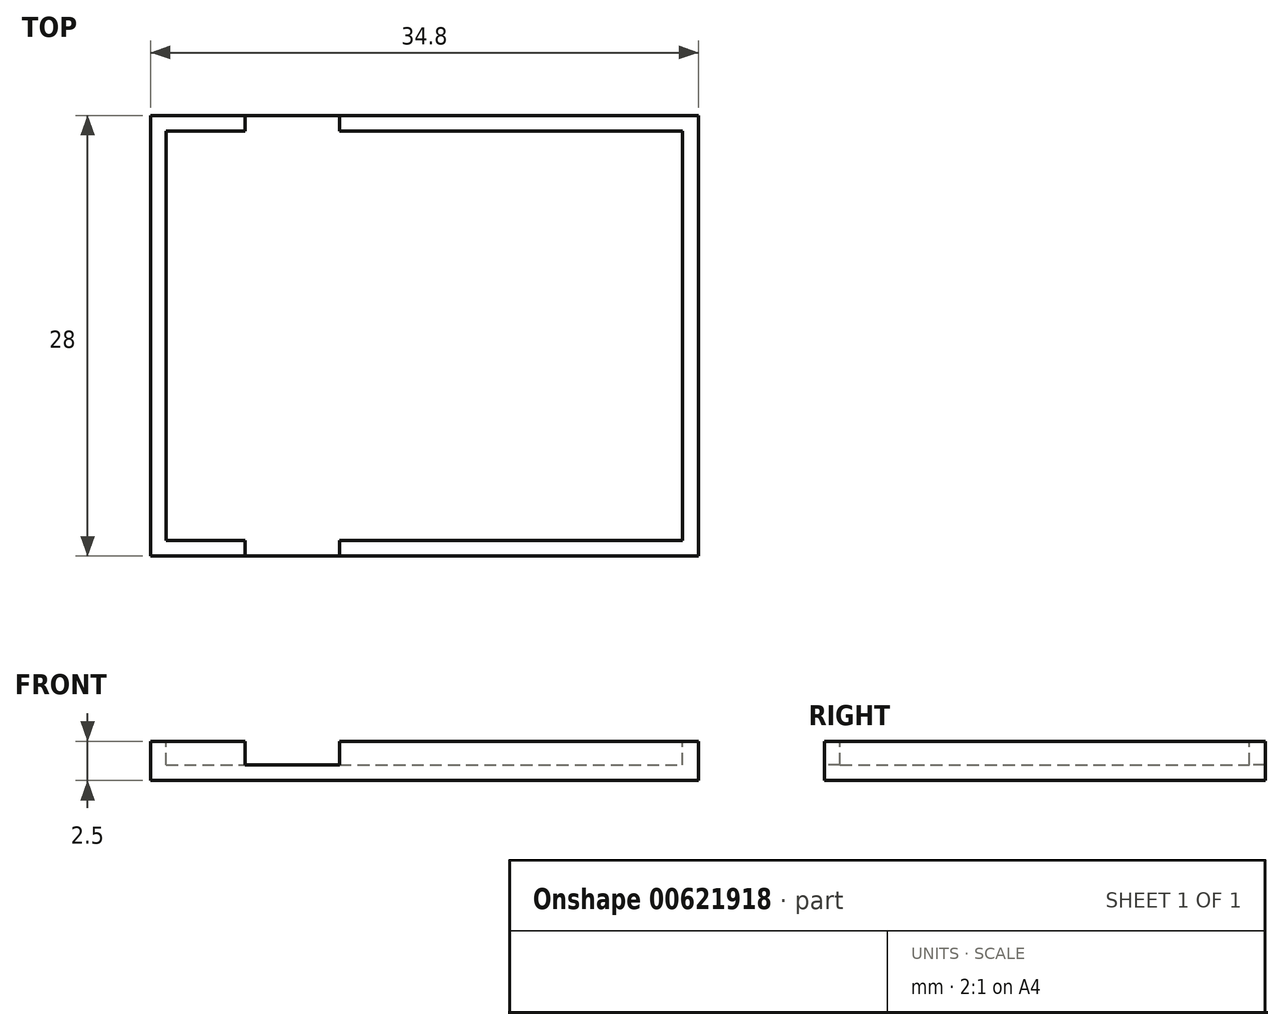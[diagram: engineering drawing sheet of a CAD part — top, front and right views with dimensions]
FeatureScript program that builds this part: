
annotation { "Feature Type Name" : "Feature", "Feature Type Description" : "" }
export const myFeature = defineFeature(function(context is Context, id is Id, definition is map)
    precondition{}
    {
        {
            var Q0;
            Q0=qCreatedBy(makeId("Top.planeOp"),FACE);
            var sketch = newSketch(context, id + "F0", { "sketchPlane" : qUnion([Q0])});
            skLineSegment(sketch, "E0.bottom", {"start": v(-17.4, -14) * mm, "end": v(17.4, -14) * mm});
            skLineSegment(sketch, "E0.top", {"start": v(-17.4, 14) * mm, "end": v(17.4, 14) * mm});
            skLineSegment(sketch, "E0.left", {"start": v(-17.4, -14) * mm, "end": v(-17.4, 14) * mm});
            skLineSegment(sketch, "E0.right", {"start": v(17.4, -14) * mm, "end": v(17.4, 14) * mm});
            skSolve(sketch);
        }
        {
            var Q0;
            Q0=makeQuery(id+"F0.imprint","IMPRINT",FACE,{"disambiguationData":[TD([[makeQuery(id+"F0.imprint","IMPRINT",EDGE,{"derivedFrom":sQuery(id+"F0.wireOp",EDGE,"E0.bottom")}),1.0]])]});
            extrude(context, id + "F1", {"entities" : qUnion([Q0]), "depth" : 2.5 * mm, "offsetDistance" : 25.4 * mm});
        }
        {
            var Q0;
            Q0=makeQuery(id+"F1.opExtrude","CAP_FACE",FACE,{"disambiguationData":[OSD([sQuery(id+"F0.wireOp",EDGE,"E0.bottom"),sQuery(id+"F0.wireOp",EDGE,"E0.top"),sQuery(id+"F0.wireOp",EDGE,"E0.left"),sQuery(id+"F0.wireOp",EDGE,"E0.right")])],"isStart":false});
            var sketch = newSketch(context, id + "F2", { "sketchPlane" : qUnion([Q0])});
            skLineSegment(sketch, "E1.bottom", {"start": v(-16.4, -13) * mm, "end": v(16.4, -13) * mm});
            skLineSegment(sketch, "E1.top", {"start": v(-16.4, 13) * mm, "end": v(16.4, 13) * mm});
            skLineSegment(sketch, "E1.left", {"start": v(-16.4, -13) * mm, "end": v(-16.4, 13) * mm});
            skLineSegment(sketch, "E1.right", {"start": v(16.4, -13) * mm, "end": v(16.4, 13) * mm});
            skSolve(sketch);
        }
        {
            var Q0;
            Q0 = qSketchRegion(id + "F2", true);
            extrude(context, id + "F3", {"entities" : qUnion([Q0]), "operationType" : NewBodyOperationType.REMOVE, "oppositeDirection" : true, "depth" : 1.5 * mm, "offsetDistance" : 25.4 * mm});
        }
        {
            var Q0;
            Q0=makeQuery(id+"F3.boolean.opBoolean","COPY",FACE,{"derivedFrom":makeQuery(id+"F3.opExtrude","CAP_FACE",FACE,{"disambiguationData":[OSD([sQuery(id+"F2.wireOp",EDGE,"E1.bottom"),sQuery(id+"F2.wireOp",EDGE,"E1.top"),sQuery(id+"F2.wireOp",EDGE,"E1.left"),sQuery(id+"F2.wireOp",EDGE,"E1.right")])],"isStart":false})});
            var sketch = newSketch(context, id + "F4", { "sketchPlane" : qUnion([Q0])});
            skLineSegment(sketch, "E2.bottom", {"start": v(-11.4, 14) * mm, "end": v(-5.4, 14) * mm});
            skLineSegment(sketch, "E2.top", {"start": v(-11.4, -14) * mm, "end": v(-5.4, -14) * mm});
            skLineSegment(sketch, "E2.left", {"start": v(-11.4, 14) * mm, "end": v(-11.4, -14) * mm});
            skLineSegment(sketch, "E2.right", {"start": v(-5.4, 14) * mm, "end": v(-5.4, -14) * mm});
            skSolve(sketch);
        }
        {
            var Q0;
            Q0 = qSketchRegion(id + "F4", true);
            extrude(context, id + "F5", {"entities" : qUnion([Q0]), "operationType" : NewBodyOperationType.REMOVE, "oppositeDirection" : true, "depth" : -1.5 * mm, "offsetDistance" : 25.4 * mm});
        }
    });
